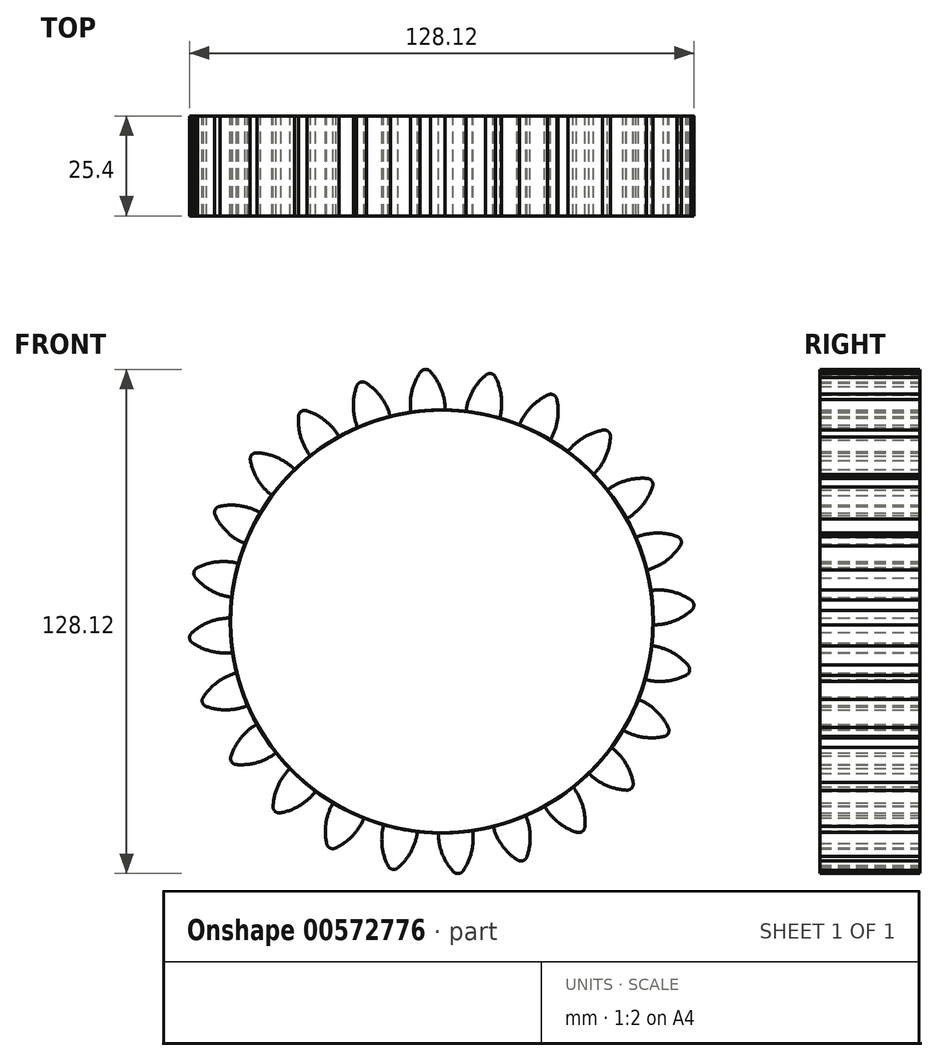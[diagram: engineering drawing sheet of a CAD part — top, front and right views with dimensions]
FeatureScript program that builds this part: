
annotation { "Feature Type Name" : "Feature", "Feature Type Description" : "" }
export const myFeature = defineFeature(function(context is Context, id is Id, definition is map)
    precondition{}
    {
        {
            var Q0;
            Q0=qCreatedBy(makeId("Front.planeOp"),FACE);
            var sketch = newSketch(context, id + "F0", { "sketchPlane" : qUnion([Q0])});
            skCircle(sketch, "E0", {"center": v(0, 0) * mm, "radius": 53.72 * mm});
            skCircle(sketch, "E1", {"center": v(0, 0) * mm, "radius": 58.67 * mm, "construction": true});
            skCircle(sketch, "E2", {"center": v(0, 0) * mm, "radius": 63.5 * mm, "construction": true});
            skPoint(sketch, "E3.endSnap0", {"position": v(0, 48.21) * mm});
            skLineSegment(sketch, "E4", {"start": v(0, 0) * mm, "end": v(-6.34, 96.78) * mm, "construction": true});
            skLineSegment(sketch, "E5", {"start": v(0, 0) * mm, "end": v(0, 96.75) * mm, "construction": true});
            skLineSegment(sketch, "E6", {"start": v(0, 58.67) * mm, "end": v(-83.05, 59.98) * mm, "construction": true});
            skLineSegment(sketch, "E7", {"start": v(0, 58.67) * mm, "end": v(-86.65, 28.67) * mm, "construction": true});
            skCircle(sketch, "E8", {"center": v(0, 0) * mm, "radius": 55.44 * mm, "construction": true});
            skCircle(sketch, "E9", {"center": v(0, 58.67) * mm, "radius": 14.6 * mm, "construction": true});
            skCircle(sketch, "E10", {"center": v(-13.74, 53.72) * mm, "radius": 14.6 * mm, "construction": true});
            skArc(sketch, "E11", {"start": v(0, 58.67) * mm, "mid": v(-1.2, 61.2) * mm, "end": v(-2.84, 63.44) * mm});
            skArc(sketch, "E12", {"start": v(0.87, 53.71) * mm, "mid": v(0.65, 56.23) * mm, "end": v(0, 58.67) * mm});
            skArc(sketch, "E13.MirrorCS", {"start": v(-7.66, 58.17) * mm, "mid": v(-6.8, 60.82) * mm, "end": v(-5.47, 63.26) * mm});
            skArc(sketch, "E14.MirrorCS", {"start": v(-7.87, 53.14) * mm, "mid": v(-7.98, 55.67) * mm, "end": v(-7.66, 58.17) * mm});
            skArc(sketch, "E15", {"start": v(-2.84, 63.44) * mm, "mid": v(-4.2, 64.06) * mm, "end": v(-5.47, 63.26) * mm});
            skSolve(sketch);
        }
        {
            var Q0;
            {var subQ0=sQuery(id+"F0.wireOp",EDGE,"E0");var subQ1=makeQuery(id+"F0.imprint","INTERSECT",VERTEX,{"derivedFrom":[subQ0,sQuery(id+"F0.wireOp",EDGE,"E12")]});Q0=makeQuery(id+"F0.imprint","IMPRINT",FACE,{"disambiguationData":[TD([[makeQuery(id+"F0.imprint","IMPRINT",EDGE,{"disambiguationData":[TD([[subQ1,-1.0]])],"derivedFrom":subQ0}),1.0]])]});}
            var Q1;
            Q1=makeQuery(id+"F0.imprint","IMPRINT",FACE,{"disambiguationData":[TD([[makeQuery(id+"F0.imprint","IMPRINT",EDGE,{"derivedFrom":sQuery(id+"F0.wireOp",EDGE,"E11")}),1.0]])]});
            extrude(context, id + "F1", {"entities" : qUnion([Q0, Q1]), "depth" : 25.4 * mm, "offsetDistance" : 25.4 * mm});
        }
        {
            var Q0;
            Q0=makeQuery(id+"F1.opExtrude","SWEPT_BODY",BODY,{"disambiguationData":[OSD([sQuery(id+"F0.wireOp",EDGE,"E0"),sQuery(id+"F0.wireOp",EDGE,"E11"),sQuery(id+"F0.wireOp",EDGE,"E12"),sQuery(id+"F0.wireOp",EDGE,"E13.MirrorCS"),sQuery(id+"F0.wireOp",EDGE,"E14.MirrorCS"),sQuery(id+"F0.wireOp",EDGE,"E15")])]});
            var Q1;
            Q1=makeQuery(id+"F1.opExtrude","SWEPT_FACE",FACE,{"disambiguationData":[OSD([sQuery(id+"F0.wireOp",EDGE,"E0")])]});
            circularPattern(context, id + "F2", {"entities" : qUnion([Q0]), "axis" : qUnion([Q1]), "angle" : 360 * degree, "instanceCount" : 24, "equalSpace" : true});
        }
    });
